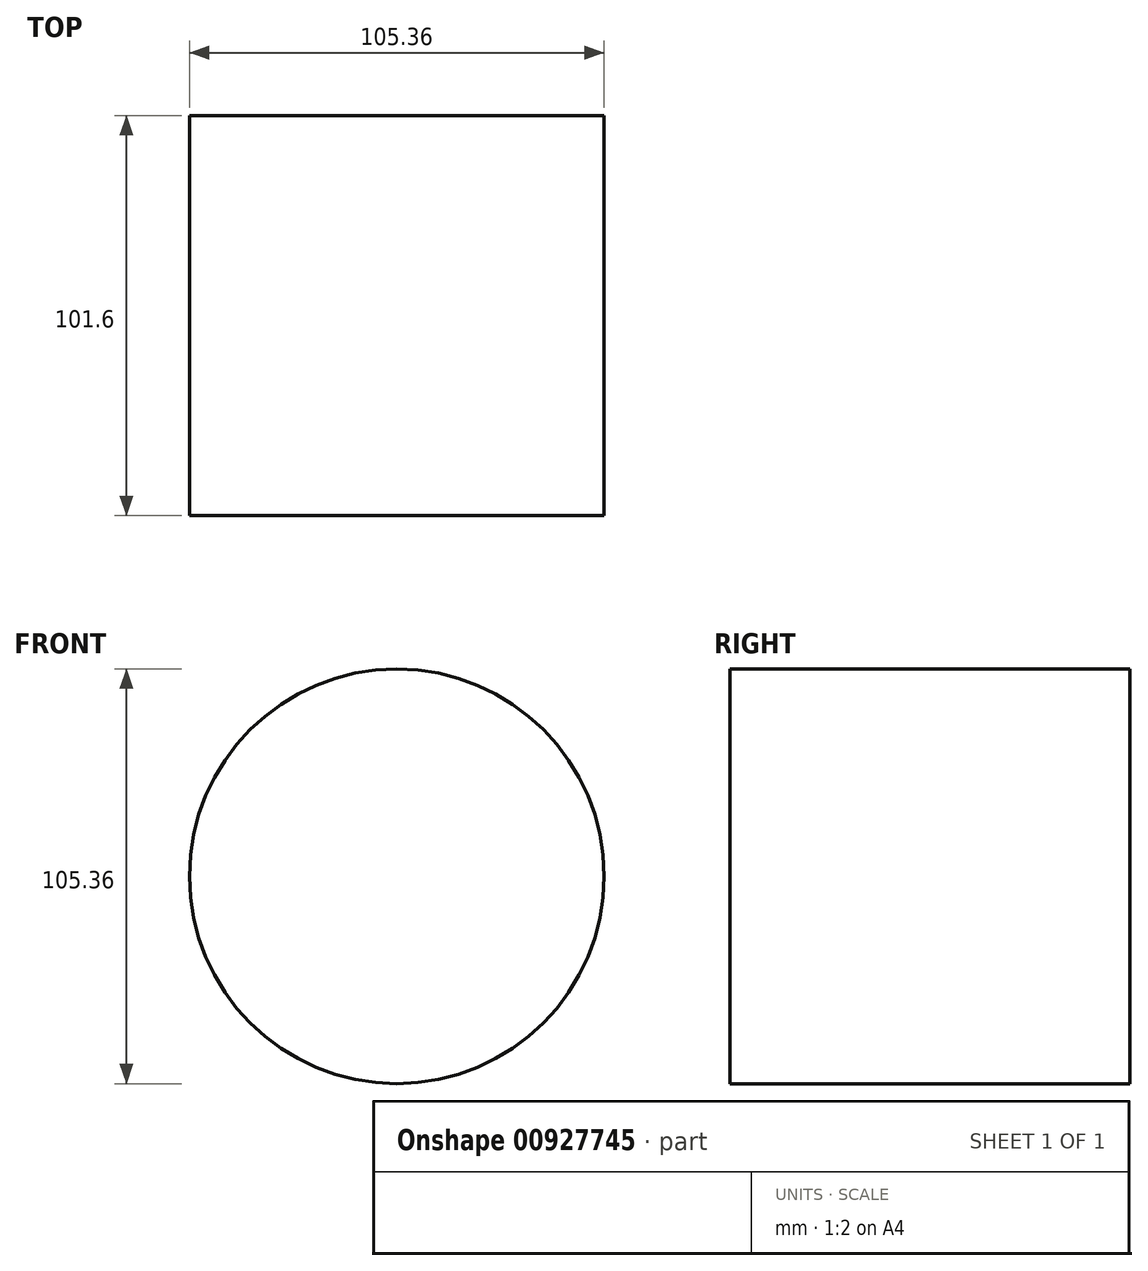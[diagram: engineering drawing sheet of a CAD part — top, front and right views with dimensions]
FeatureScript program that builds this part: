
annotation { "Feature Type Name" : "Feature", "Feature Type Description" : "" }
export const myFeature = defineFeature(function(context is Context, id is Id, definition is map)
    precondition{}
    {
        {
            var Q0;
            Q0=qCreatedBy(makeId("Front.planeOp"),FACE);
            var sketch = newSketch(context, id + "F0", { "sketchPlane" : qUnion([Q0])});
            skCircle(sketch, "E0", {"center": v(0, 0) * mm, "radius": 52.68 * mm});
            skSolve(sketch);
        }
        {
            var Q0;
            Q0=makeQuery(id+"F0.imprint","IMPRINT",FACE,{"disambiguationData":[TD([[makeQuery(id+"F0.imprint","IMPRINT",EDGE,{"derivedFrom":sQuery(id+"F0.wireOp",EDGE,"E0")}),1.0]])]});
            var Q1;
            Q1=sQuery(id+"F0.wireOp",EDGE,"E0");
            extrude(context, id + "F1", {"entities" : qUnion([Q0]), "surfaceEntities" : qUnion([Q1]), "endBound" : BoundingType.SYMMETRIC, "depth" : 101.6 * mm, "offsetDistance" : 25.4 * mm});
        }
    });
